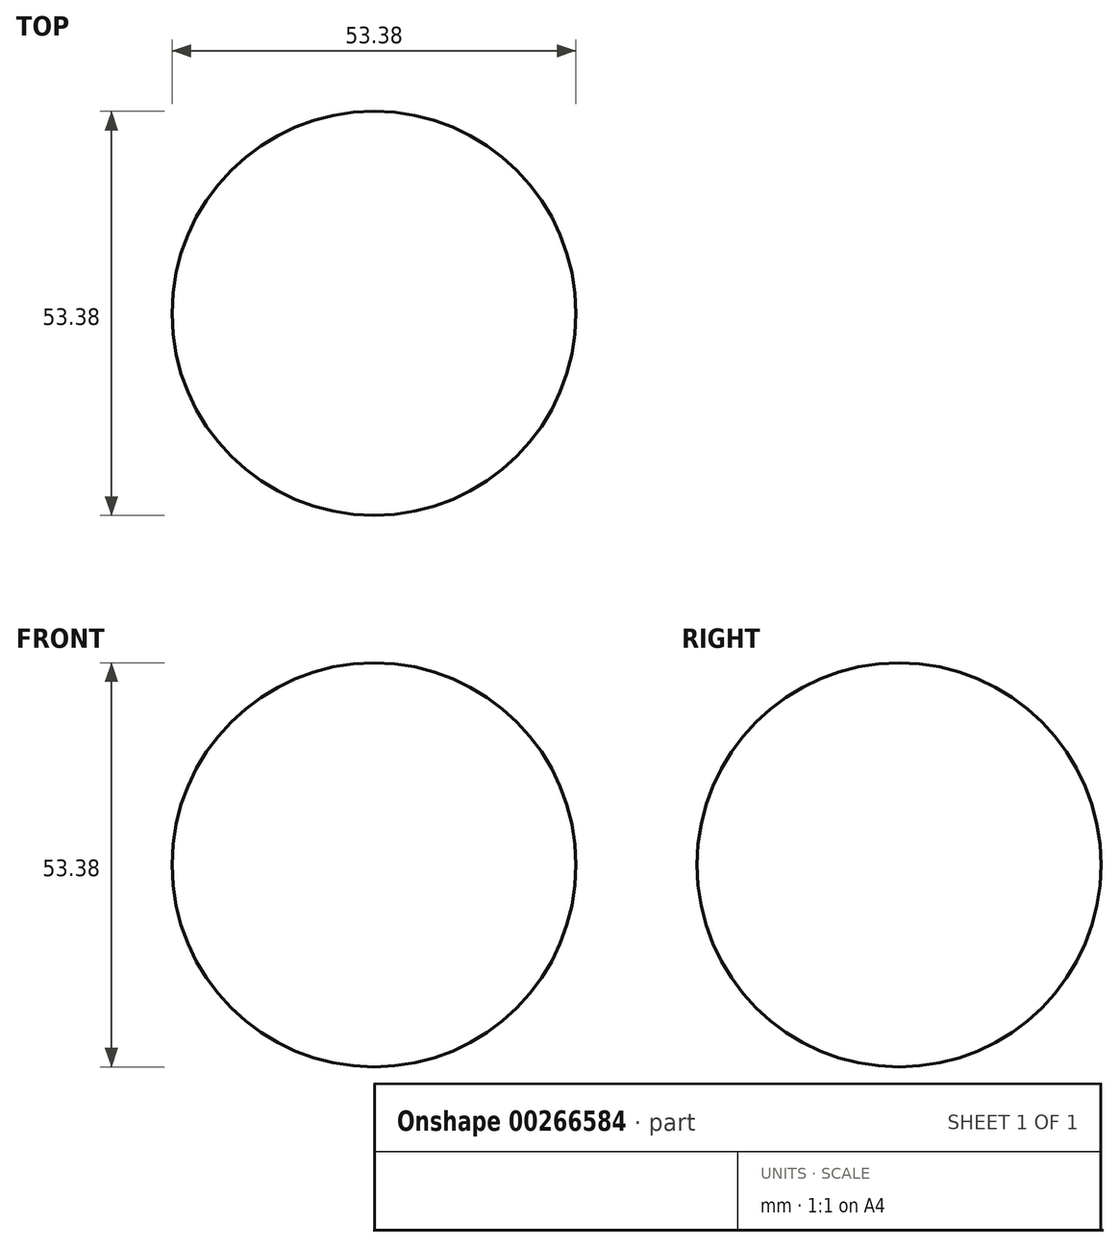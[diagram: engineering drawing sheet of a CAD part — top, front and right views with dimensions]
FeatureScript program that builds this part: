
annotation { "Feature Type Name" : "Feature", "Feature Type Description" : "" }
export const myFeature = defineFeature(function(context is Context, id is Id, definition is map)
    precondition{}
    {
        {
            var Q0;
            Q0=qCreatedBy(makeId("Top.planeOp"),FACE);
            var sketch = newSketch(context, id + "F0", { "sketchPlane" : qUnion([Q0])});
            skArc(sketch, "E0", {"start": v(0, -26.7) * mm, "mid": v(26.7, 0) * mm, "end": v(0, 26.7) * mm});
            skLineSegment(sketch, "E1", {"start": v(0, -26.7) * mm, "end": v(0, 26.7) * mm});
            skSolve(sketch);
        }
        {
            var Q0;
            Q0=makeQuery(id+"F0.imprint","IMPRINT",FACE,{"disambiguationData":[TD([[makeQuery(id+"F0.imprint","IMPRINT",EDGE,{"derivedFrom":sQuery(id+"F0.wireOp",EDGE,"E0")}),1.0]])]});
            var Q1;
            Q1=sQuery(id+"F0.wireOp",EDGE,"E1");
            revolve(context, id + "F1", {"entities" : qUnion([Q0]), "axis" : qUnion([Q1]), "revolveType" : RevolveType.FULL});
        }
    });
